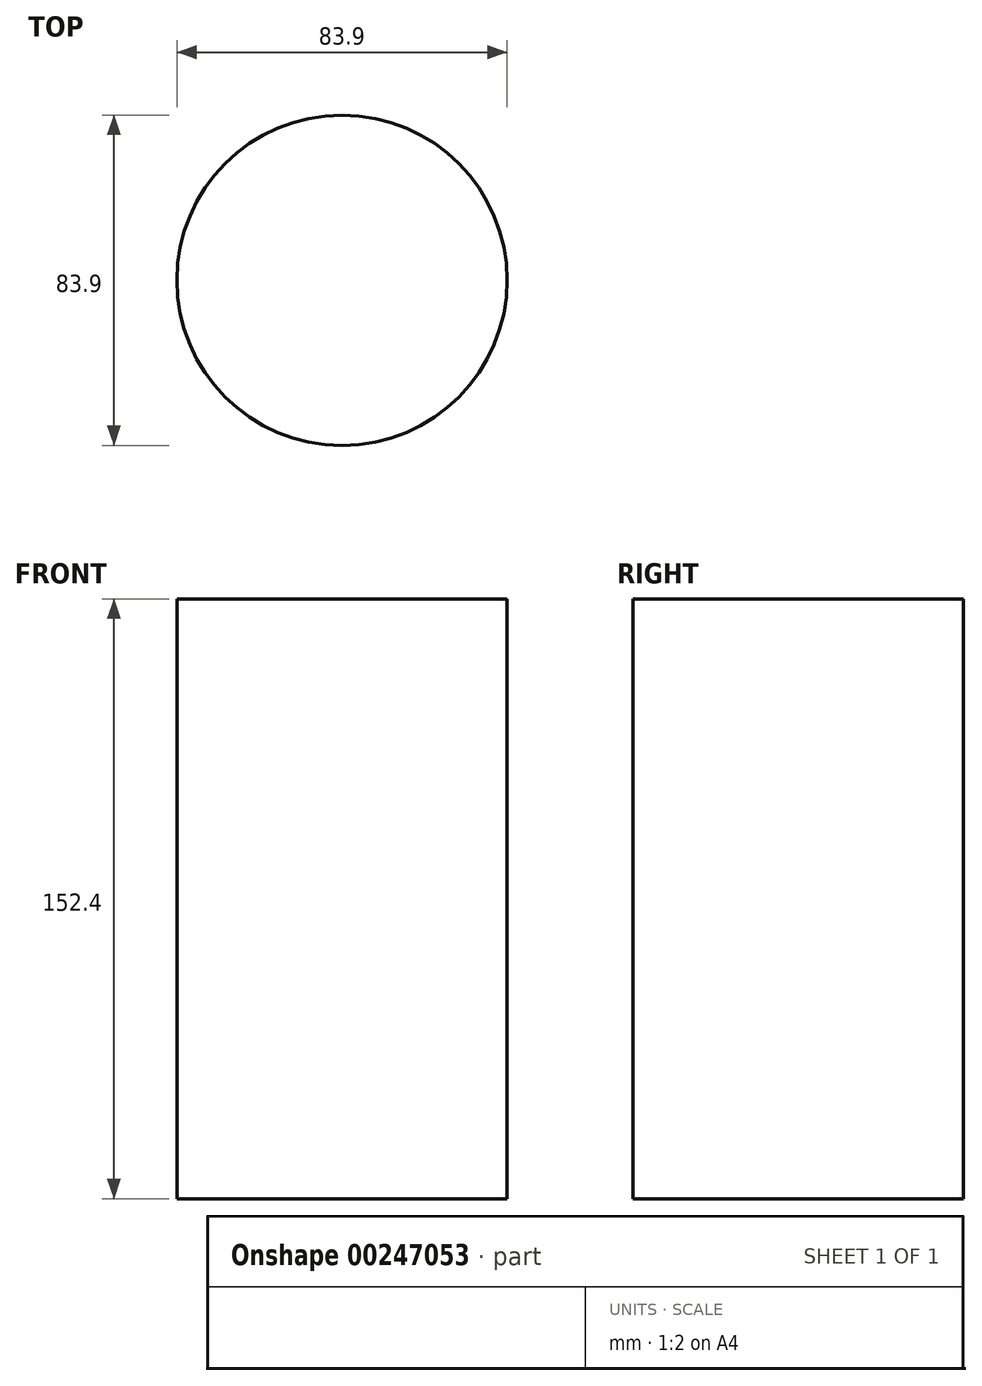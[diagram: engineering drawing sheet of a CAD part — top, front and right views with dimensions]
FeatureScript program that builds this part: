
annotation { "Feature Type Name" : "Feature", "Feature Type Description" : "" }
export const myFeature = defineFeature(function(context is Context, id is Id, definition is map)
    precondition{}
    {
        {
            var Q0;
            Q0=qCreatedBy(makeId("Top.planeOp"),FACE);
            var sketch = newSketch(context, id + "F0", { "sketchPlane" : qUnion([Q0])});
            skCircle(sketch, "E0", {"center": v(0, 0) * mm, "radius": 41.95 * mm});
            skSolve(sketch);
        }
        {
            var Q0;
            Q0 = qSketchRegion(id + "F0", true);
            extrude(context, id + "F1", {"entities" : qUnion([Q0]), "depth" : 152.4 * mm});
        }
    });
